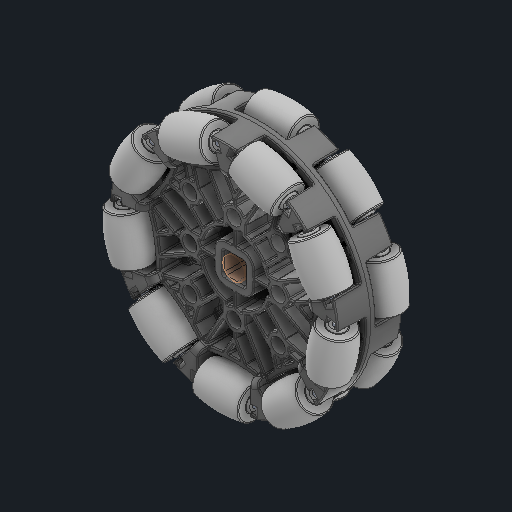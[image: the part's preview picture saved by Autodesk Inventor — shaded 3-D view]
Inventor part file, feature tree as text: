
AUTODESK INVENTOR PART (.ipt)
format: ipt  version: 2025 (Build 290162000, 162)  size: 28,591,616 bytes
history: native  units: in
note: dims shown in document units (in); Inventor stores cm internally (conversion verified against a paired STEP export)
features: other x59, sketch x1
ambient origin geometry x8: Origin, YZ Plane, XZ Plane, XY Plane, X Axis, Y Axis, Z Axis, Center Point
bodies: Solid1 (feature_tree), Solid2 (feature_tree), Solid3 (feature_tree), Solid4 (feature_tree), Solid5 (feature_tree), Solid6 (feature_tree), Solid7 (feature_tree), Solid8 (feature_tree), Solid9 (feature_tree), Solid10 (feature_tree), Solid11 (feature_tree), Solid12 (feature_tree), Solid13 (feature_tree), Solid14 (feature_tree), Solid15 (feature_tree), Solid16 (feature_tree), Solid17 (feature_tree), Solid18 (feature_tree), Solid19 (feature_tree), Solid20 (feature_tree), Solid21 (feature_tree), Solid22 (feature_tree), Solid23 (feature_tree), Solid24 (feature_tree), Solid25 (feature_tree), Solid26 (feature_tree), Solid27 (feature_tree), Solid28 (feature_tree), Solid29 (feature_tree), Solid30 (feature_tree), Solid31 (feature_tree), Solid32 (feature_tree), Solid33 (feature_tree), Solid34 (feature_tree), Solid35 (feature_tree), Solid36 (feature_tree), Solid37 (feature_tree), Solid38 (feature_tree), Solid39 (feature_tree), Solid40 (feature_tree), Solid41 (feature_tree), Solid42 (feature_tree), Solid43 (feature_tree), Solid44 (feature_tree), Solid45 (feature_tree), Solid46 (feature_tree), Solid47 (feature_tree), Solid48 (feature_tree), Solid49 (feature_tree), Solid50 (feature_tree), Solid51 (feature_tree), Solid52 (feature_tree), Solid53 (feature_tree), Solid54 (feature_tree), Solid55 (feature_tree)
feature tree (60):
  other  "2.75 Omni Antistatic.ipt"
  other  "Solid1::2.75 Omni Antistatic.ipt"
  other  "Solid2::2.75 Omni Antistatic.ipt"
  other  "Solid3::2.75 Omni Antistatic.ipt"
  other  "Solid4::2.75 Omni Antistatic.ipt"
  other  "Solid5::2.75 Omni Antistatic.ipt"
  other  "Solid6::2.75 Omni Antistatic.ipt"
  other  "Solid7::2.75 Omni Antistatic.ipt"
  other  "Solid8::2.75 Omni Antistatic.ipt"
  other  "Solid9::2.75 Omni Antistatic.ipt"
  other  "Solid10::2.75 Omni Antistatic.ipt"
  other  "Solid11::2.75 Omni Antistatic.ipt"
  other  "Solid12::2.75 Omni Antistatic.ipt"
  other  "Solid13::2.75 Omni Antistatic.ipt"
  other  "Solid14::2.75 Omni Antistatic.ipt"
  other  "Solid15::2.75 Omni Antistatic.ipt"
  other  "Solid16::2.75 Omni Antistatic.ipt"
  other  "Solid17::2.75 Omni Antistatic.ipt"
  other  "Solid18::2.75 Omni Antistatic.ipt"
  other  "Solid19::2.75 Omni Antistatic.ipt"
  other  "Solid20::2.75 Omni Antistatic.ipt"
  other  "Solid21::2.75 Omni Antistatic.ipt"
  other  "Solid22::2.75 Omni Antistatic.ipt"
  other  "Solid23::2.75 Omni Antistatic.ipt"
  other  "Solid24::2.75 Omni Antistatic.ipt"
  other  "Solid25::2.75 Omni Antistatic.ipt"
  other  "Solid26::2.75 Omni Antistatic.ipt"
  other  "Solid27::2.75 Omni Antistatic.ipt"
  other  "Solid28::2.75 Omni Antistatic.ipt"
  other  "Solid29::2.75 Omni Antistatic.ipt"
  other  "Solid30::2.75 Omni Antistatic.ipt"
  other  "Solid31::2.75 Omni Antistatic.ipt"
  other  "Solid32::2.75 Omni Antistatic.ipt"
  other  "Solid33::2.75 Omni Antistatic.ipt"
  other  "Solid34::2.75 Omni Antistatic.ipt"
  other  "Solid35::2.75 Omni Antistatic.ipt"
  other  "Solid36::2.75 Omni Antistatic.ipt"
  other  "Solid37::2.75 Omni Antistatic.ipt"
  other  "Solid38::2.75 Omni Antistatic.ipt"
  other  "Solid39::2.75 Omni Antistatic.ipt"
  other  "Solid40::2.75 Omni Antistatic.ipt"
  other  "Solid41::2.75 Omni Antistatic.ipt"
  other  "Solid42::2.75 Omni Antistatic.ipt"
  other  "Solid43::2.75 Omni Antistatic.ipt"
  other  "Solid44::2.75 Omni Antistatic.ipt"
  other  "Solid45::2.75 Omni Antistatic.ipt"
  other  "Solid46::2.75 Omni Antistatic.ipt"
  other  "Solid47::2.75 Omni Antistatic.ipt"
  other  "Solid48::2.75 Omni Antistatic.ipt"
  other  "Solid49::2.75 Omni Antistatic.ipt"
  other  "Solid50::2.75 Omni Antistatic.ipt"
  other  "Solid51::2.75 Omni Antistatic.ipt"
  other  "Solid52::2.75 Omni Antistatic.ipt"
  other  "Solid53::2.75 Omni Antistatic.ipt"
  other  "Solid54::2.75 Omni Antistatic.ipt"
  other  "Solid55::2.75 Omni Antistatic.ipt"
  other  "TaggingFeature1"
  sketch  "Sketch1"  dims[d0=0.3937in]
  other  "Srf1"
  other  "Srf1::Derived"
